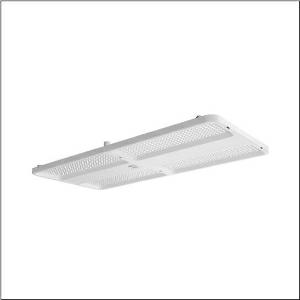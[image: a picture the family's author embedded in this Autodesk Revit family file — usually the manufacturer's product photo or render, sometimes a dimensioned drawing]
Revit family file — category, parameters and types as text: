
# Revit family: highbay_11_maxi_51hn12db4mda01
name_source: partatom
category: Lighting Fixtures
units: mm (PartAtom-declared; Revit-internal decimal feet)

## family parameters
Cut with Voids When Loaded = No
Host = Face
Light Source = No
Part Type = Normal
Room Calculation Point = No
Round Connector Dimension = Use Diameter
Shared = No

## types (1)
- --- (1 x LED, 30000 lm, 147 W, 4000K)
    Apparent Load = 147 VA
    CIE Flux Codes = 87 98 100 100 100
    Color Rendering = 80
    Color Temperature = 4000K
    Default Elevation = 1800 mm
    Description = high bay luminaire Highbay 11 maxi; direct symmetric wide distribution, light control with lens of PMMA; UGR ≤ 22 (X = 4H | Y = 8H | S = 0.25H | reflection values 70/50/20); luminous flux: 30.000lm; light colour: 840, colour temperature: 4000K, MacAdam ≤ 2 SDCM (initial), colour rendering: CRI > 80; luminous efficacy: 204,1lm/W; rated service life: 100.000h (L95/B50) at AT= 25°C; control: Bluetooth® Mesh; for wireless networking: Node multi-sensor luminaire for setting up a local control solution without a higher-level application controller, intelligence completely integrated into the luminaire; with auto-swarm function: leading lighting creates safety. The function is already active without any „out-of-the-box“ commissioning; commissioning is not necessary thanks to „out-of-the-box“ functions: basic functions (presence lighting, follow-up times, fading times, etc.) are already preset at the factory; no control line such as DALI between the Node multi-sensor luminaires and Nodes is required, wireless integration of other Node luminaires and Node multi-sensor luminaires into the network is possible; number of Node multi-sensor luminaires in the project can be expanded as required, network sizes > 300 Nodes can be realized; can also be connected to lighting or building automation via various gateways upon request; integrated DALI2 ECG provides luminaire data (according to IEC62386, Part 251), energy data (Part 252), and monitoring and analytics data (Part 253) to higher-level systems for further processing; luminaire with PIR sensor (passive-infrared); with light sensor; luminaire connection: terminal, 5-pole, max. 2.5mm² (cable entry for one cable, Ø 8.5..16mm); mains connection: 230..240V, AC 50/60Hz; connected load: 147W; protection rating (complete): IP65; insulation class (complete): insulation class I (protective earthing); protection symbol: D; certification: CE, ENEC, VDE, UKCA; internal wiring halogen-free; luminaire corresponds to IFS (International Featured Standards) requirements for safety and quality in the food industry; LABS conformity tested according to VDMA 24364:2018-05; housing frame of high-performance plastic PA6, matt traffic white (RAL 9016); cover of PMMA; dimension (LxWxH): 946 x 442 x 72mm; permissible operating ambient temperature: -20..+40°C (reducing of maximum allowable ambient temperature of 5°C with ceiling mounting); packaging unit: 1 piece; (delivery without accessories; please order mounting accessories separately)
    Height = 72 mm  [stored 0.23622 ft]
    Lamp = 1 x LED
    Lamp Light Flux = 30000 lm
    Lamp Power = 147 W
    Lamp count = 1
    Length = 946 mm
    Luminous efficacy = 204 lm/W
    Manufacturer = Siteco
    ModVariant = No
    Model = 51HN12DB4MDA01
    Mounting Place = Ceiling
    Mounting Type = Pendant
    Number of Poles = 1
    OnlyDefault = Yes
    Power Factor = 1
    Product Name = Highbay 11 maxi
    Product group = high bay luminaire
    ProductGroupID = 901
    Protection Class = Protection class I
    Protection Degree = IP 65
    RLX_Detail_Level = 1
    RLX_Emergency_Light_Flux = 0 lm
    RLX_Emergency_Type = 0
    RLX_Emergency_Type_DB = No
    RlxData = <blob elided: 127749 chars, md5=480e17f3>
    Socket = socket
    Standby Power = 0 W
    System Light Flux = 30000 lm
    System Power = 147 W
    Type Comments = factory setting: luminous flux: 100 % | dim-lin: 254 | 679 mA
    Type Image = l_1363267.jpg
    URL = http://relux.com
    VarID = @adj_013939
    Voltage = 0 V
    Weight = 0.00 kg
    Width = 442 mm

note: [stored X ft] marks values corroborated as IEEE doubles in the binary element streams (Revit-internal decimal feet)

## geometry (parser evidence)
native form markers: Blend x4, Sweep x12
no freeform markers — native parametric forms only
